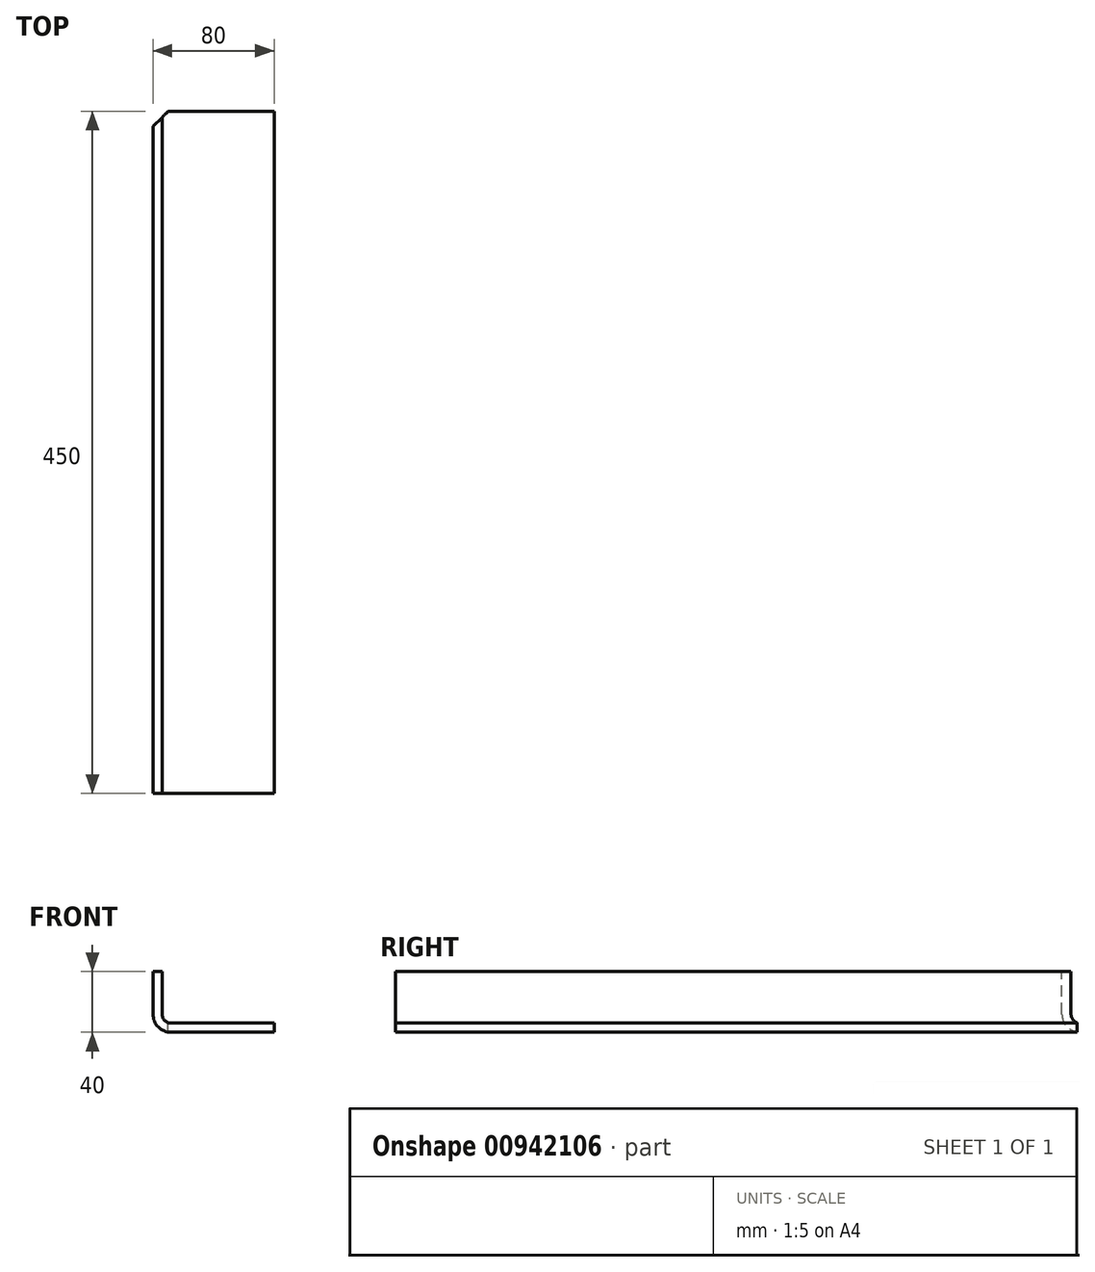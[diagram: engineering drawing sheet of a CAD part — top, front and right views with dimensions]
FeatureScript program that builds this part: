
annotation { "Feature Type Name" : "Feature", "Feature Type Description" : "" }
export const myFeature = defineFeature(function(context is Context, id is Id, definition is map)
    precondition{}
    {
        {
            var Q0;
            Q0=qCreatedBy(makeId("Front.planeOp"),FACE);
            var sketch = newSketch(context, id + "F0", { "sketchPlane" : qUnion([Q0])});
            skLineSegment(sketch, "E0", {"start": v(0, 40) * mm, "end": v(0, 12) * mm});
            skLineSegment(sketch, "E1", {"start": v(12, 0) * mm, "end": v(80, 0) * mm});
            skLineSegment(sketch, "E2", {"start": v(80, 0) * mm, "end": v(80, 6) * mm});
            skLineSegment(sketch, "E3", {"start": v(80, 6) * mm, "end": v(12, 6) * mm});
            skLineSegment(sketch, "E4", {"start": v(6, 12) * mm, "end": v(6, 40) * mm});
            skLineSegment(sketch, "E5", {"start": v(6, 40) * mm, "end": v(0, 40) * mm});
            skPoint(sketch, "E6.visualSharp", {"position": v(6, 6) * mm});
            skArc(sketch, "E6.filletArc", {"start": v(6, 12) * mm, "mid": v(7.76, 7.76) * mm, "end": v(12, 6) * mm});
            skPoint(sketch, "E7.visualSharp", {"position": v(0, 0) * mm});
            skArc(sketch, "E7.filletArc", {"start": v(0, 12) * mm, "mid": v(3.51, 3.51) * mm, "end": v(12, 0) * mm});
            skSolve(sketch);
        }
        {
            var Q0;
            Q0=makeQuery(id+"F0.imprint","IMPRINT",FACE,{"disambiguationData":[TD([[makeQuery(id+"F0.imprint","IMPRINT",EDGE,{"derivedFrom":sQuery(id+"F0.wireOp",EDGE,"E0")}),1.0]])]});
            extrude(context, id + "F1", {"entities" : qUnion([Q0]), "depth" : 450 * mm, "offsetDistance" : 25 * mm});
        }
        {
            var Q0;
            Q0=makeQuery(id+"F1.opExtrude","SWEPT_FACE",FACE,{"disambiguationData":[OSD([sQuery(id+"F0.wireOp",EDGE,"E5")])]});
            var sketch = newSketch(context, id + "F2", { "sketchPlane" : qUnion([Q0])});
            skLineSegment(sketch, "E8", {"start": v(0, -10) * mm, "end": v(10, 0) * mm});
            skLineSegment(sketch, "E9", {"start": v(10, 0) * mm, "end": v(0, 0) * mm});
            skLineSegment(sketch, "E10", {"start": v(0, 0) * mm, "end": v(0, -10) * mm});
            skSolve(sketch);
        }
        {
            var Q0;
            Q0 = qSketchRegion(id + "F2", true);
            extrude(context, id + "F3", {"entities" : qUnion([Q0]), "operationType" : NewBodyOperationType.REMOVE, "endBound" : BoundingType.THROUGH_ALL, "oppositeDirection" : true, "depth" : 25 * mm, "offsetDistance" : 25 * mm});
        }
    });
